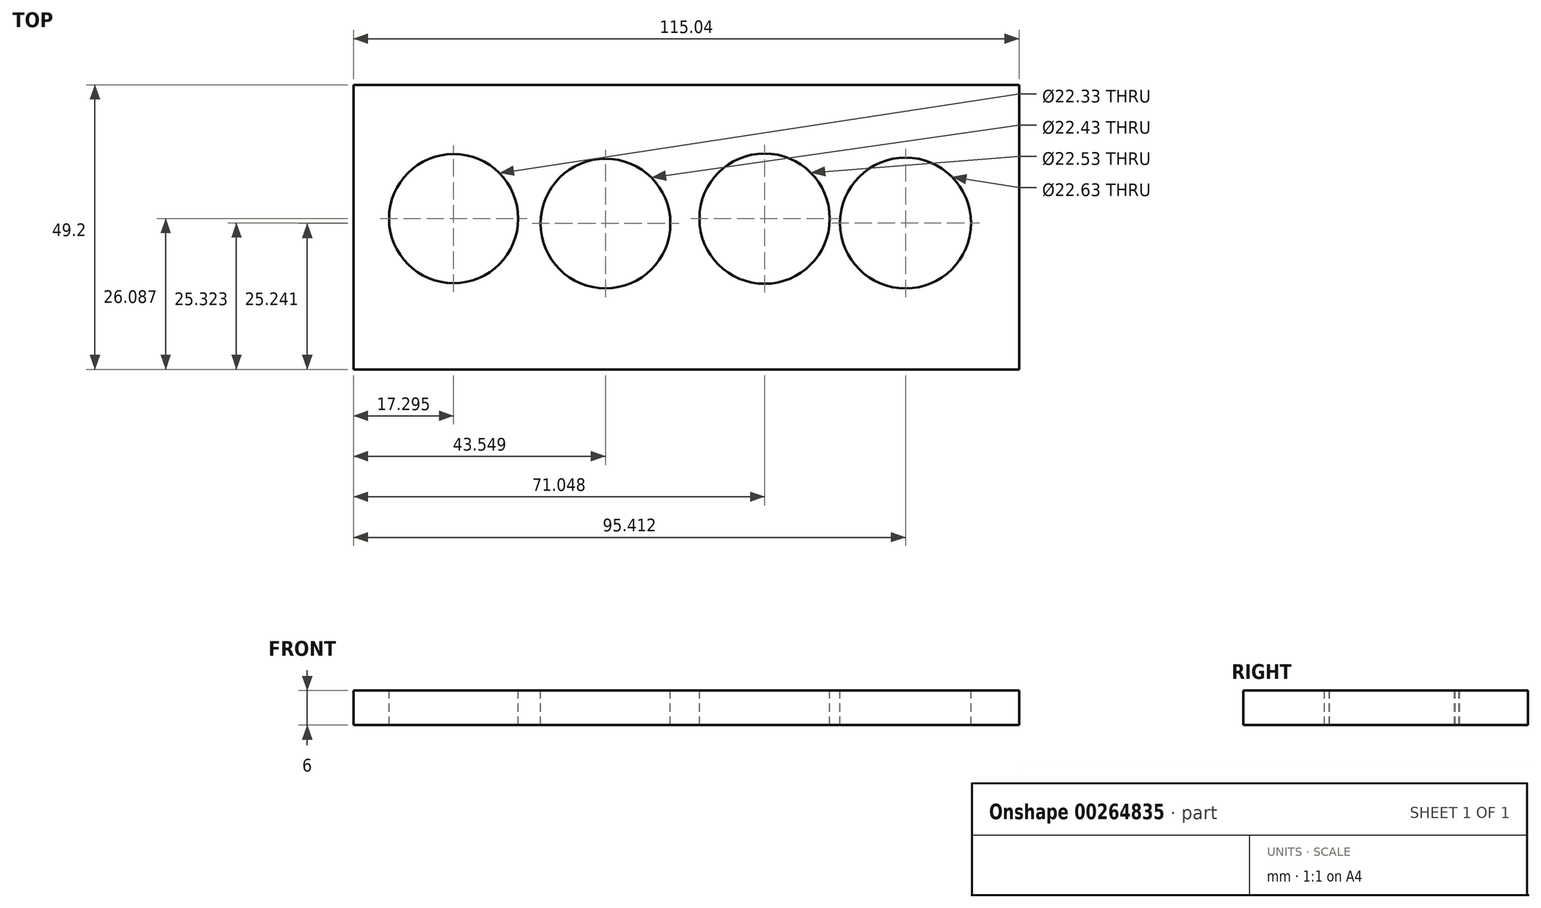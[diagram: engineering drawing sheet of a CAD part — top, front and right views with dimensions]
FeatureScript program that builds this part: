
annotation { "Feature Type Name" : "Feature", "Feature Type Description" : "" }
export const myFeature = defineFeature(function(context is Context, id is Id, definition is map)
    precondition{}
    {
        {
            var Q0;
            Q0=qCreatedBy(makeId("Top.planeOp"),FACE);
            var sketch = newSketch(context, id + "F0", { "sketchPlane" : qUnion([Q0])});
            skLineSegment(sketch, "E0.bottom", {"start": v(-58.08, 28) * mm, "end": v(56.96, 28) * mm});
            skLineSegment(sketch, "E0.top", {"start": v(-58.08, -21.2) * mm, "end": v(56.96, -21.2) * mm});
            skLineSegment(sketch, "E0.left", {"start": v(-58.08, 28) * mm, "end": v(-58.08, -21.2) * mm});
            skLineSegment(sketch, "E0.right", {"start": v(56.96, 28) * mm, "end": v(56.96, -21.2) * mm});
            skSolve(sketch);
        }
        {
            var Q0;
            Q0=makeQuery(id+"F0.imprint","IMPRINT",FACE,{"disambiguationData":[TD([[makeQuery(id+"F0.imprint","IMPRINT",EDGE,{"derivedFrom":sQuery(id+"F0.wireOp",EDGE,"E0.bottom")}),-1.0]])]});
            extrude(context, id + "F1", {"entities" : qUnion([Q0]), "depth" : 6 * mm});
        }
        {
            var Q0;
            Q0=makeQuery(id+"F1.opExtrude","CAP_FACE",FACE,{"disambiguationData":[OSD([sQuery(id+"F0.wireOp",EDGE,"E0.bottom"),sQuery(id+"F0.wireOp",EDGE,"E0.top"),sQuery(id+"F0.wireOp",EDGE,"E0.left"),sQuery(id+"F0.wireOp",EDGE,"E0.right")])],"isStart":false});
            var sketch = newSketch(context, id + "F2", { "sketchPlane" : qUnion([Q0])});
            skLineSegment(sketch, "E1", {"start": v(-53.57, 4.89) * mm, "end": v(-25.75, 4.89) * mm});
            skLineSegment(sketch, "E2", {"start": v(-25.75, 4.89) * mm, "end": v(-40.78, 14.85) * mm});
            skLineSegment(sketch, "E3", {"start": v(-40.78, 14.85) * mm, "end": v(-40.78, 4.89) * mm});
            skLineSegment(sketch, "E4", {"start": v(-40.78, 4.89) * mm, "end": v(-40.78, -9.59) * mm});
            skLineSegment(sketch, "E5", {"start": v(-14.53, 4.04) * mm, "end": v(-18.56, 4.04) * mm});
            skLineSegment(sketch, "E6", {"start": v(-18.56, 4.04) * mm, "end": v(-3.57, 17.1) * mm});
            skLineSegment(sketch, "E7", {"start": v(-16.7, 16.73) * mm, "end": v(-12.37, -8.65) * mm});
            skLineSegment(sketch, "E8", {"start": v(-14.53, 4.04) * mm, "end": v(4.12, 5.45) * mm});
            skLineSegment(sketch, "E9", {"start": v(12.97, 4.89) * mm, "end": v(12.97, 13.66) * mm});
            skLineSegment(sketch, "E10", {"start": v(12.97, 13.66) * mm, "end": v(21.43, 5.07) * mm});
            skLineSegment(sketch, "E11", {"start": v(21.43, 5.07) * mm, "end": v(12.97, 4.89) * mm});
            skLineSegment(sketch, "E12", {"start": v(37.33, 4.12) * mm, "end": v(37.33, 13.7) * mm});
            skSolve(sketch);
        }
        {
            var Q0;
            Q0=sQuery(id+"F2.wireOp",VERTEX,"E4.start");
            var Q1;
            Q1=makeQuery(id+"F1.opExtrude","SWEPT_BODY",BODY,{"disambiguationData":[OSD([sQuery(id+"F0.wireOp",EDGE,"E0.bottom"),sQuery(id+"F0.wireOp",EDGE,"E0.top"),sQuery(id+"F0.wireOp",EDGE,"E0.left"),sQuery(id+"F0.wireOp",EDGE,"E0.right")])]});
            hole(context, id + "F3", {"style" : HoleStyle.C_SINK, "endStyle" : HoleEndStyle.THROUGH, "holeDiameter" : 22.33 * mm, "cSinkDiameter" : 22.33 * mm, "cSinkAngle" : 90 * degree, "isTappedThrough" : true, "tappedDepth" : 12 * mm, "tapClearance" : 3, "locations" : qUnion([Q0]), "scope" : qUnion([Q1])});
        }
        {
            var Q0;
            Q0=sQuery(id+"F2.wireOp",VERTEX,"E8.start");
            var Q1;
            Q1=makeQuery(id+"F1.opExtrude","SWEPT_BODY",BODY,{"disambiguationData":[OSD([sQuery(id+"F0.wireOp",EDGE,"E0.bottom"),sQuery(id+"F0.wireOp",EDGE,"E0.top"),sQuery(id+"F0.wireOp",EDGE,"E0.left"),sQuery(id+"F0.wireOp",EDGE,"E0.right")])]});
            hole(context, id + "F4", {"style" : HoleStyle.C_SINK, "endStyle" : HoleEndStyle.THROUGH, "holeDiameter" : 22.43 * mm, "cSinkDiameter" : 22.43 * mm, "cSinkAngle" : 90 * degree, "isTappedThrough" : true, "tappedDepth" : 12 * mm, "tapClearance" : 3, "locations" : qUnion([Q0]), "scope" : qUnion([Q1])});
        }
        {
            var Q0;
            Q0=sQuery(id+"F2.wireOp",VERTEX,"E9.start");
            var Q1;
            Q1=makeQuery(id+"F1.opExtrude","SWEPT_BODY",BODY,{"disambiguationData":[OSD([sQuery(id+"F0.wireOp",EDGE,"E0.bottom"),sQuery(id+"F0.wireOp",EDGE,"E0.top"),sQuery(id+"F0.wireOp",EDGE,"E0.left"),sQuery(id+"F0.wireOp",EDGE,"E0.right")])]});
            hole(context, id + "F5", {"style" : HoleStyle.C_SINK, "endStyle" : HoleEndStyle.THROUGH, "holeDiameter" : 22.53 * mm, "cSinkDiameter" : 22.53 * mm, "cSinkAngle" : 90 * degree, "isTappedThrough" : true, "tappedDepth" : 12 * mm, "tapClearance" : 3, "locations" : qUnion([Q0]), "scope" : qUnion([Q1])});
        }
        {
            var Q0;
            Q0=sQuery(id+"F2.wireOp",VERTEX,"E12.start");
            var Q1;
            Q1=makeQuery(id+"F1.opExtrude","SWEPT_BODY",BODY,{"disambiguationData":[OSD([sQuery(id+"F0.wireOp",EDGE,"E0.bottom"),sQuery(id+"F0.wireOp",EDGE,"E0.top"),sQuery(id+"F0.wireOp",EDGE,"E0.left"),sQuery(id+"F0.wireOp",EDGE,"E0.right")])]});
            hole(context, id + "F6", {"style" : HoleStyle.C_SINK, "endStyle" : HoleEndStyle.THROUGH, "holeDiameter" : 22.63 * mm, "cSinkDiameter" : 22.63 * mm, "cSinkAngle" : 90 * degree, "isTappedThrough" : true, "tappedDepth" : 12 * mm, "tapClearance" : 3, "locations" : qUnion([Q0]), "scope" : qUnion([Q1])});
        }
    });
